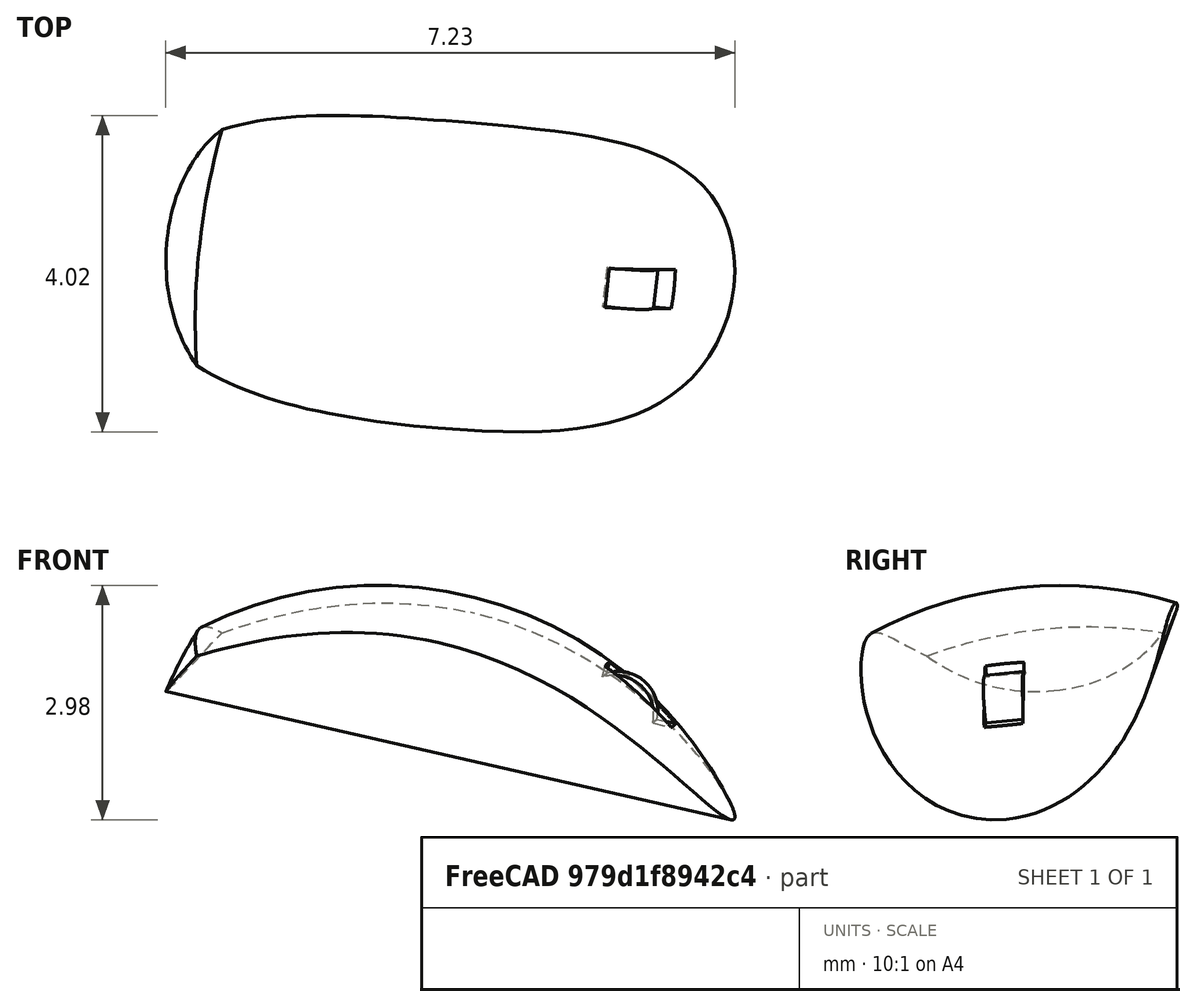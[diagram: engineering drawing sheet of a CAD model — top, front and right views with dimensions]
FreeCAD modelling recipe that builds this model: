
FCSTD DOCUMENT  (FreeCAD 0.15R4671 (Git))
Label: post_test_model
License: All rights reserved
LicenseURL: http://en.wikipedia.org/wiki/All_rights_reserved
objects: Part::Sphere×2, Part::Cylinder×2, Part::Common×2, Part::Box×1, Part::Cut×1, Part::MultiFuse×1
note: 9 computed .brp shape members not serialized (recipe doc carries the construction recipe); baked Part::Feature solids carry a one-line shape summary decoded from their .brp

FEATURE [Part::Sphere] Sphere
  Angle1 = -90
  Angle2 = 90
  Angle3 = 360
  Radius = 5
FEATURE [Part::Cylinder] Cylinder
  Angle = 360
  Height = 10
  Placement = pos=(-5,0,5) rot=(0,1,0;1.5708rad)
  Radius = 2
FEATURE [Part::Common] Common
  Base = -> Sphere
  Tool = -> Cylinder
FEATURE [Part::Sphere] Sphere001
  Angle1 = -90
  Angle2 = 90
  Angle3 = 360
  Placement = pos=(2,-0.00115234,2) rot=(0.740234,-0.656342,0.145841;1.84607rad)
  Radius = 5.5
FEATURE [Part::Common] Common001
  Base = -> Sphere001
  Tool = -> Common
FEATURE [Part::Box] Box  label="Cube"
  Height = 4
  Length = 1
  Placement = pos=(2,-0.25,4) rot=(0,0,1;0rad)
  Width = 0.5
FEATURE [Part::Cut] Cut
  Base = -> Common001
  Tool = -> Box
FEATURE [Part::Cylinder] Cylinder001
  Angle = 360
  Height = 0.5
  Placement = pos=(2.25,0.25,4) rot=(1,0,0;1.5708rad)
  Radius = 0.5
FEATURE [Part::MultiFuse] Fusion
  Placement = pos=(0,0,0) rot=(0.416104,0.834053,-0.362235;0.261339rad)
  Shapes = -> [Cut,Cylinder001]
